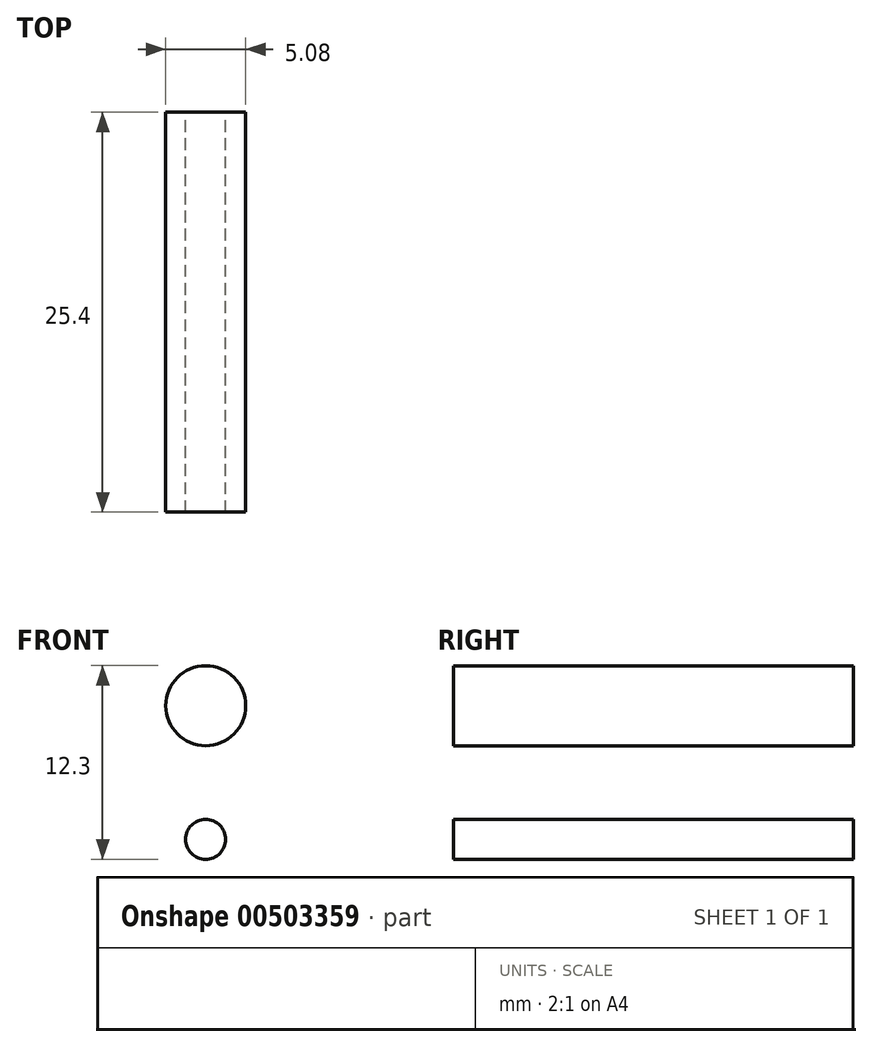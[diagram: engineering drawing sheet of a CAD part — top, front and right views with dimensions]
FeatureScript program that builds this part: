
annotation { "Feature Type Name" : "Feature", "Feature Type Description" : "" }
export const myFeature = defineFeature(function(context is Context, id is Id, definition is map)
    precondition{}
    {
        {
            var Q0;
            Q0=qCreatedBy(makeId("Front.planeOp"),FACE);
            var sketch = newSketch(context, id + "F0", { "sketchPlane" : qUnion([Q0])});
            skCircle(sketch, "E0", {"center": v(0, 0) * mm, "radius": 1.27 * mm});
            skCircle(sketch, "E1", {"center": v(0, 8.49) * mm, "radius": 2.54 * mm});
            skSolve(sketch);
        }
        {
            var Q0;
            Q0=makeQuery(id+"F0.imprint","IMPRINT",FACE,{"disambiguationData":[TD([[makeQuery(id+"F0.imprint","IMPRINT",EDGE,{"derivedFrom":sQuery(id+"F0.wireOp",EDGE,"E1")}),1.0]])]});
            var Q1;
            Q1=makeQuery(id+"F0.imprint","IMPRINT",FACE,{"disambiguationData":[TD([[makeQuery(id+"F0.imprint","IMPRINT",EDGE,{"derivedFrom":sQuery(id+"F0.wireOp",EDGE,"E0")}),1.0]])]});
            extrude(context, id + "F1", {"entities" : qUnion([Q0, Q1]), "depth" : 25.4 * mm});
        }
    });
